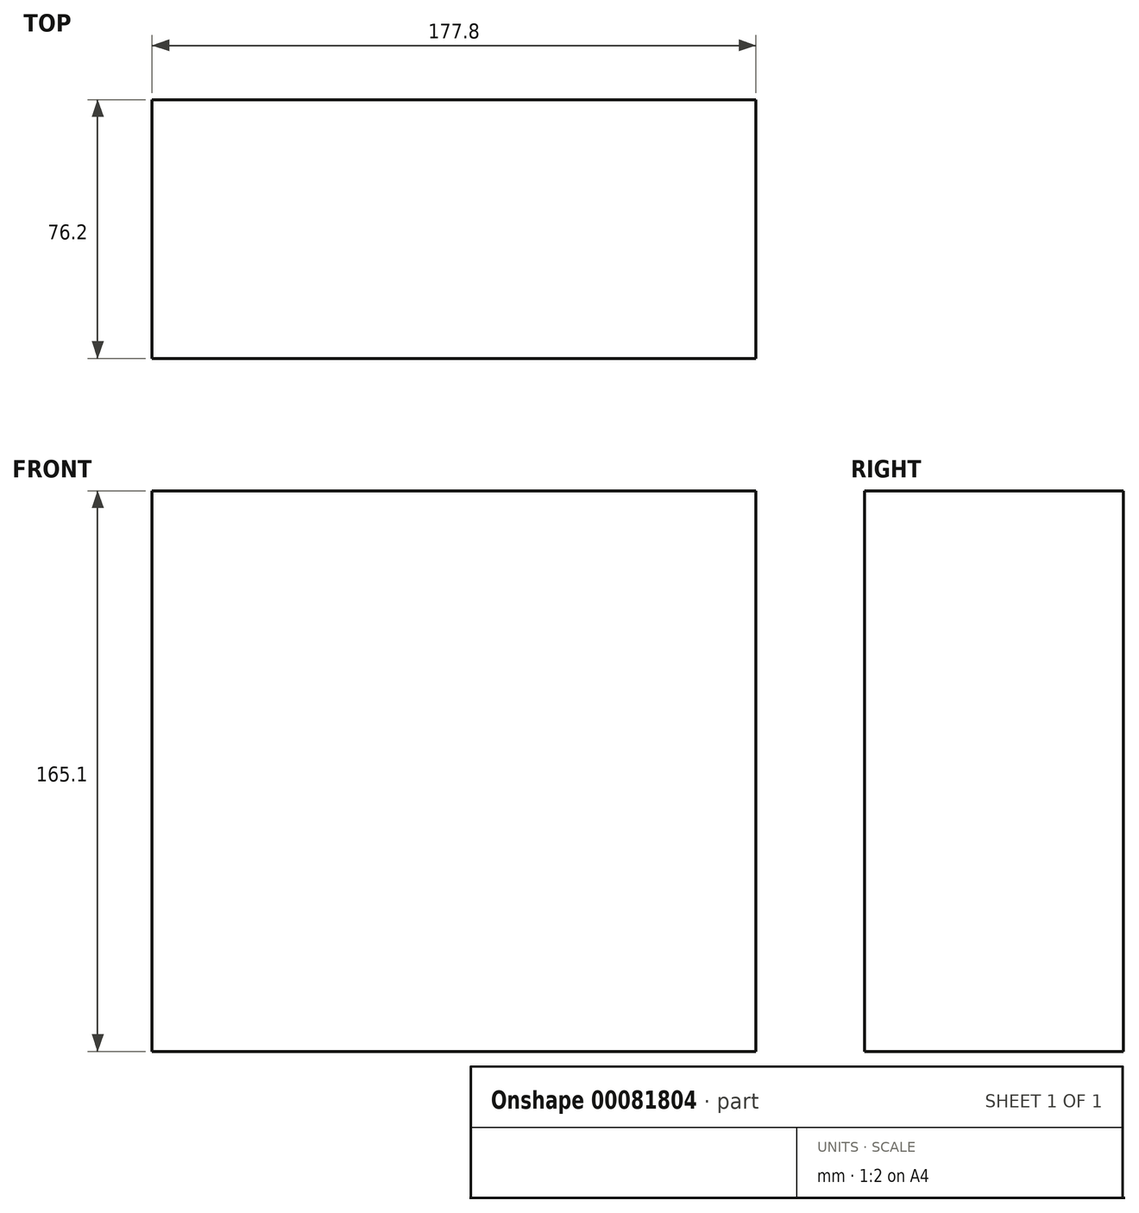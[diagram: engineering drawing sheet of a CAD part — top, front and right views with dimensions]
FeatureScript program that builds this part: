
annotation { "Feature Type Name" : "Feature", "Feature Type Description" : "" }
export const myFeature = defineFeature(function(context is Context, id is Id, definition is map)
    precondition{}
    {
        {
            var Q0;
            Q0=qCreatedBy(makeId("Top.planeOp"),FACE);
            var sketch = newSketch(context, id + "F0", { "sketchPlane" : qUnion([Q0])});
            skLineSegment(sketch, "E0.bottom", {"start": v(-88.9, 29.08) * mm, "end": v(88.9, 29.08) * mm});
            skLineSegment(sketch, "E0.top", {"start": v(-88.9, -47.12) * mm, "end": v(88.9, -47.12) * mm});
            skLineSegment(sketch, "E0.left", {"start": v(-88.9, 29.08) * mm, "end": v(-88.9, -47.12) * mm});
            skLineSegment(sketch, "E0.right", {"start": v(88.9, 29.08) * mm, "end": v(88.9, -47.12) * mm});
            skSolve(sketch);
        }
        {
            var Q0;
            Q0=makeQuery(id+"F0.imprint","IMPRINT",FACE,{"disambiguationData":[TD([[makeQuery(id+"F0.imprint","IMPRINT",EDGE,{"derivedFrom":sQuery(id+"F0.wireOp",EDGE,"E0.bottom")}),-1.0]])]});
            extrude(context, id + "F1", {"entities" : qUnion([Q0]), "depth" : 165.1 * mm});
        }
    });
